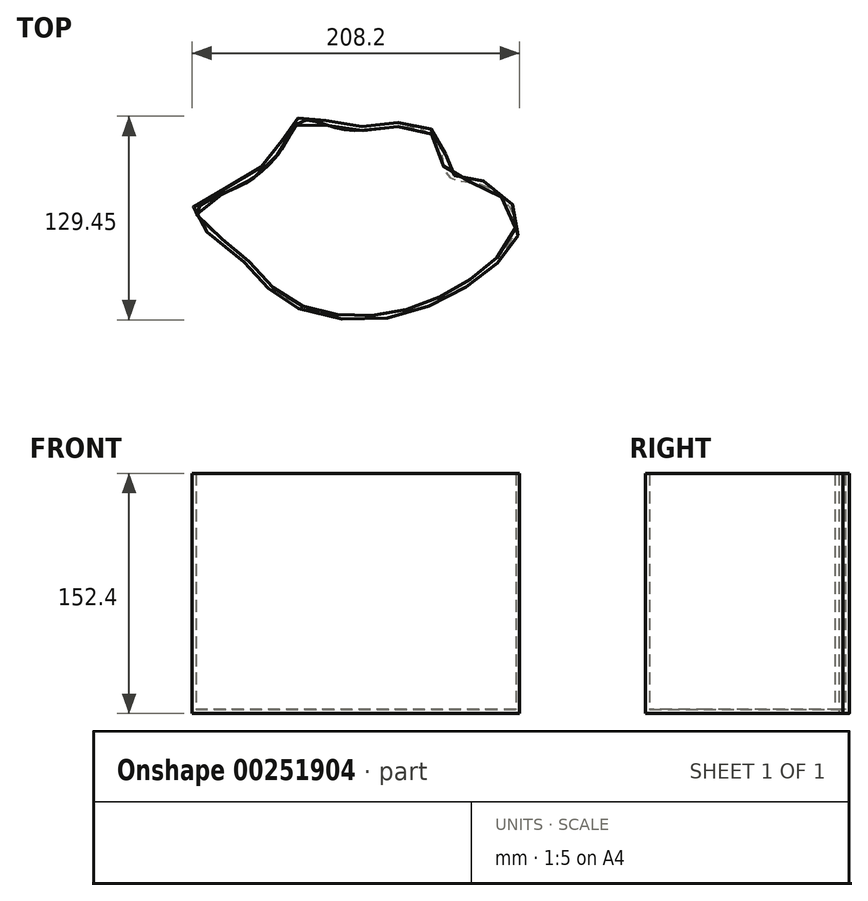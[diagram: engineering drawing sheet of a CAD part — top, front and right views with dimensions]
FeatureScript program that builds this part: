
annotation { "Feature Type Name" : "Feature", "Feature Type Description" : "" }
export const myFeature = defineFeature(function(context is Context, id is Id, definition is map)
    precondition{}
    {
        {
            var Q0;
            Q0=qCreatedBy(makeId("Top.planeOp"),FACE);
            var sketch = newSketch(context, id + "F0", { "sketchPlane" : qUnion([Q0])});
            skPoint(sketch, "E0.middle", {"position": v(0, 0) * mm});
            skPoint(sketch, "E1.visualSharp", {"position": v(-76.2, 50.8) * mm});
            skPoint(sketch, "E2.visualSharp", {"position": v(76.2, 50.8) * mm});
            skPoint(sketch, "E3.visualSharp", {"position": v(76.2, -50.8) * mm});
            skPoint(sketch, "E4.visualSharp", {"position": v(-76.2, -50.8) * mm});
            skFitSpline(sketch, "E5", {"points": [v(-50.8, 50.8) * mm, v(-38.56, 65.84) * mm, v(-9.64, 59.99) * mm, v(26.85, 62.05) * mm, v(50.8, 50.8) * mm, v(56.12, 30.03) * mm, v(76.2, 25.4) * mm, v(99.84, 0) * mm, v(87.45, -25.4) * mm, v(50.8, -50.8) * mm, v(0, -63.27) * mm, v(-50.8, -50.8) * mm, v(-76.2, -25.4) * mm, v(-108.1, 5.93) * mm, v(-76.2, 25.4) * mm, v(-50.8, 50.8) * mm]});
            skPoint(sketch, "E3.filletArc.end.orphan", {"position": v(76.2, -25.4) * mm});
            skSolve(sketch);
        }
        {
            var Q0;
            Q0=makeQuery(id+"F0.imprint","IMPRINT",FACE,{"disambiguationData":[TD([[makeQuery(id+"F0.imprint","IMPRINT",EDGE,{"derivedFrom":sQuery(id+"F0.wireOp",EDGE,"E5")}),-1.0]])]});
            extrude(context, id + "F1", {"entities" : qUnion([Q0]), "depth" : 152.4 * mm});
        }
        {
            var Q0;
            Q0=makeQuery(id+"F1.opExtrude","CAP_FACE",FACE,{"disambiguationData":[OSD([sQuery(id+"F0.wireOp",EDGE,"E5")])],"isStart":false});
            shell(context, id + "F2", {"entities" : qUnion([Q0]), "thickness" : 2.54 * mm});
        }
    });
